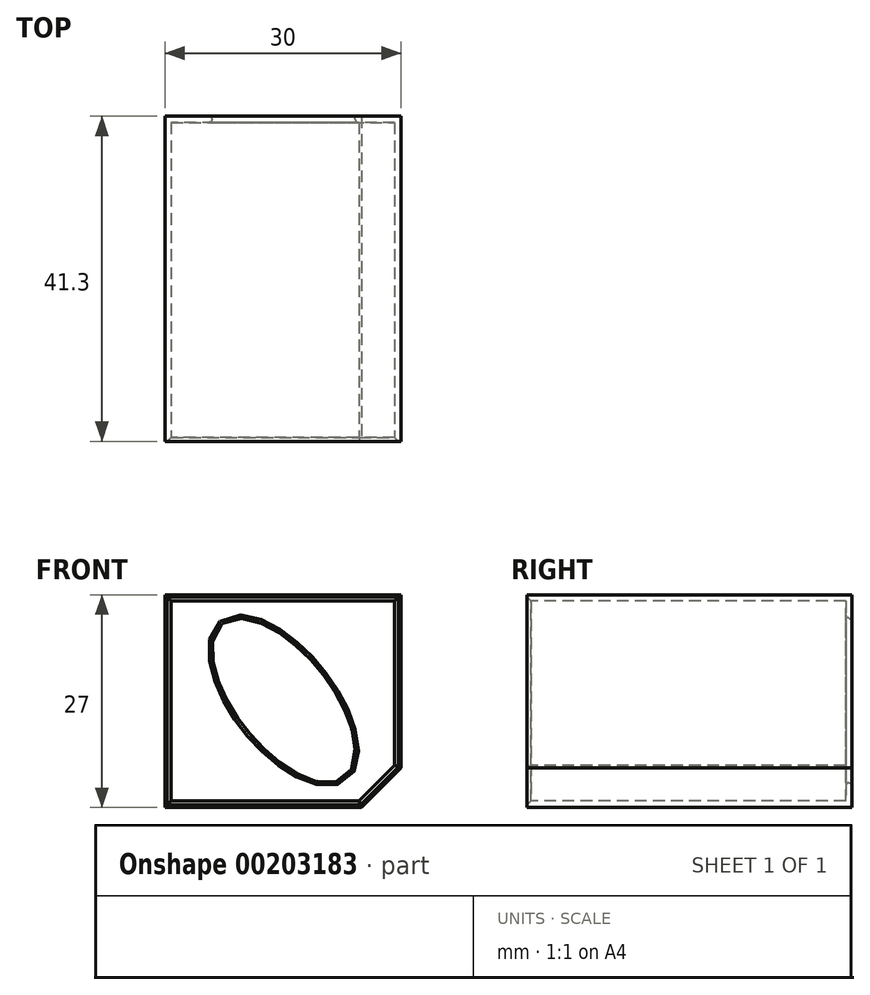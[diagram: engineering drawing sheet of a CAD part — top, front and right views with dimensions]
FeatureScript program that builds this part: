
annotation { "Feature Type Name" : "Feature", "Feature Type Description" : "" }
export const myFeature = defineFeature(function(context is Context, id is Id, definition is map)
    precondition{}
    {
        {
            assignVariable(context, id + "F0", {"name" : "epparoi", "anyValue" : 0.8});
        }
        {
            var Q0;
            Q0=qCreatedBy(makeId("Front.planeOp"),FACE);
            var sketch = newSketch(context, id + "F1", { "sketchPlane" : qUnion([Q0])});
            skLineSegment(sketch, "E0", {"start": v(0, 0) * mm, "end": v(0, 27) * mm});
            skLineSegment(sketch, "E1", {"start": v(0, 27) * mm, "end": v(30, 27) * mm});
            skLineSegment(sketch, "E2", {"start": v(30, 27) * mm, "end": v(30, 5) * mm});
            skLineSegment(sketch, "E3", {"start": v(30, 5) * mm, "end": v(25, 0) * mm});
            skLineSegment(sketch, "E4", {"start": v(25, 0) * mm, "end": v(0, 0) * mm});
            skSolve(sketch);
        }
        {
            var Q0;
            Q0=makeQuery(id+"F1.imprint","IMPRINT",FACE,{"disambiguationData":[TD([[makeQuery(id+"F1.imprint","IMPRINT",EDGE,{"derivedFrom":sQuery(id+"F1.wireOp",EDGE,"E0")}),-1.0]])]});
            extrude(context, id + "F2", {"entities" : qUnion([Q0]), "oppositeDirection" : true, "depth" : 41.3 * mm});
        }
        {
            var Q0;
            Q0=makeQuery(id+"F2.opExtrude","CAP_FACE",FACE,{"disambiguationData":[OSD([sQuery(id+"F1.wireOp",EDGE,"E0"),sQuery(id+"F1.wireOp",EDGE,"E1"),sQuery(id+"F1.wireOp",EDGE,"E2"),sQuery(id+"F1.wireOp",EDGE,"E3"),sQuery(id+"F1.wireOp",EDGE,"E4")])],"isStart":true});
            shell(context, id + "F3", {"entities" : qUnion([Q0]), "thickness" : (getVariable(context, 'epparoi')) * mm});
        }
        {
            var Q0;
            Q0=makeQuery(id+"F2.opExtrude","CAP_FACE",FACE,{"disambiguationData":[OSD([sQuery(id+"F1.wireOp",EDGE,"E0"),sQuery(id+"F1.wireOp",EDGE,"E1"),sQuery(id+"F1.wireOp",EDGE,"E2"),sQuery(id+"F1.wireOp",EDGE,"E3"),sQuery(id+"F1.wireOp",EDGE,"E4")])],"isStart":false});
            var sketch = newSketch(context, id + "F4", { "sketchPlane" : qUnion([Q0])});
            skLineSegment(sketch, "E5", {"start": v(0, 27) * mm, "end": v(-27.5, 2.5) * mm, "construction": true});
            skLineSegment(sketch, "E6", {"start": v(-30, 27) * mm, "end": v(0, 0) * mm, "construction": true});
            skEllipse(sketch, "E7", {"center": v(-15.08, 13.57) * mm, "majorRadius": 12.5 * mm, "minorRadius": 6 * mm, "majorAxis": v(0.62, 0.78)});
            skSolve(sketch);
        }
        {
            var Q0;
            Q0=makeQuery(id+"F4.imprint","IMPRINT",FACE,{"disambiguationData":[TD([[makeQuery(id+"F4.imprint","IMPRINT",EDGE,{"derivedFrom":sQuery(id+"F4.wireOp",EDGE,"E7")}),1.0]])]});
            extrude(context, id + "F5", {"entities" : qUnion([Q0]), "operationType" : NewBodyOperationType.REMOVE, "endBound" : BoundingType.THROUGH_ALL, "oppositeDirection" : true, "depth" : 25 * mm});
        }
        {
            var Q0;
            {var subQ0=sQuery(id+"F1.wireOp",EDGE,"E1");Q0=makeQuery(id+"F3.opShell","OFFSET_EDGE",EDGE,{"disambiguationData":[OSD([subQ0]),TDD([makeQuery(id+"F2.opExtrude","CAP_EDGE",EDGE,{"disambiguationData":[OSD([subQ0])],"isStart":true})])]});}
            var Q1;
            {var subQ0=sQuery(id+"F1.wireOp",EDGE,"E2");Q1=makeQuery(id+"F3.opShell","OFFSET_EDGE",EDGE,{"disambiguationData":[OSD([subQ0]),TDD([makeQuery(id+"F2.opExtrude","CAP_EDGE",EDGE,{"disambiguationData":[OSD([subQ0])],"isStart":true})])]});}
            var Q2;
            {var subQ0=sQuery(id+"F1.wireOp",EDGE,"E3");Q2=makeQuery(id+"F3.opShell","OFFSET_EDGE",EDGE,{"disambiguationData":[OSD([subQ0]),TDD([makeQuery(id+"F2.opExtrude","CAP_EDGE",EDGE,{"disambiguationData":[OSD([subQ0])],"isStart":true})])]});}
            var Q3;
            {var subQ0=sQuery(id+"F1.wireOp",EDGE,"E4");Q3=makeQuery(id+"F3.opShell","OFFSET_EDGE",EDGE,{"disambiguationData":[OSD([subQ0]),TDD([makeQuery(id+"F2.opExtrude","CAP_EDGE",EDGE,{"disambiguationData":[OSD([subQ0])],"isStart":true})])]});}
            var Q4;
            {var subQ0=sQuery(id+"F1.wireOp",EDGE,"E0");Q4=makeQuery(id+"F3.opShell","OFFSET_EDGE",EDGE,{"disambiguationData":[OSD([subQ0]),TDD([makeQuery(id+"F2.opExtrude","CAP_EDGE",EDGE,{"disambiguationData":[OSD([subQ0])],"isStart":true})])]});}
            chamfer(context, id + "F6", {"entities" : qUnion([Q0, Q1, Q2, Q3, Q4]), "width" : 0.5 * mm, "tangentPropagation" : true});
        }
        {
            var Q0;
            Q0=makeQuery(id+"F5.boolean.opBoolean","COPY",EDGE,{"derivedFrom":makeQuery(id+"F5.opExtrude","CAP_EDGE",EDGE,{"disambiguationData":[OSD([sQuery(id+"F4.wireOp",EDGE,"E7")])],"isStart":true})});
            var Q1;
            Q1=makeQuery(id+"F5.boolean.opBoolean","INTERSECT",EDGE,{"derivedFrom":[makeQuery(id+"F3.opShell","OFFSET_FACE",FACE,{"disambiguationData":[OSD([sQuery(id+"F1.wireOp",EDGE,"E0"),sQuery(id+"F1.wireOp",EDGE,"E1"),sQuery(id+"F1.wireOp",EDGE,"E2"),sQuery(id+"F1.wireOp",EDGE,"E3"),sQuery(id+"F1.wireOp",EDGE,"E4")])]}),makeQuery(id+"F5.opExtrude","SWEPT_FACE",FACE,{"disambiguationData":[OSD([sQuery(id+"F4.wireOp",EDGE,"E7")])]})]});
            fillet(context, id + "F7", {"entities" : qUnion([Q0, Q1]), "radius" : (getVariable(context, 'epparoi') / 2) * mm, "tangentPropagation" : true, "allowEdgeOverflow" : false});
        }
    });
